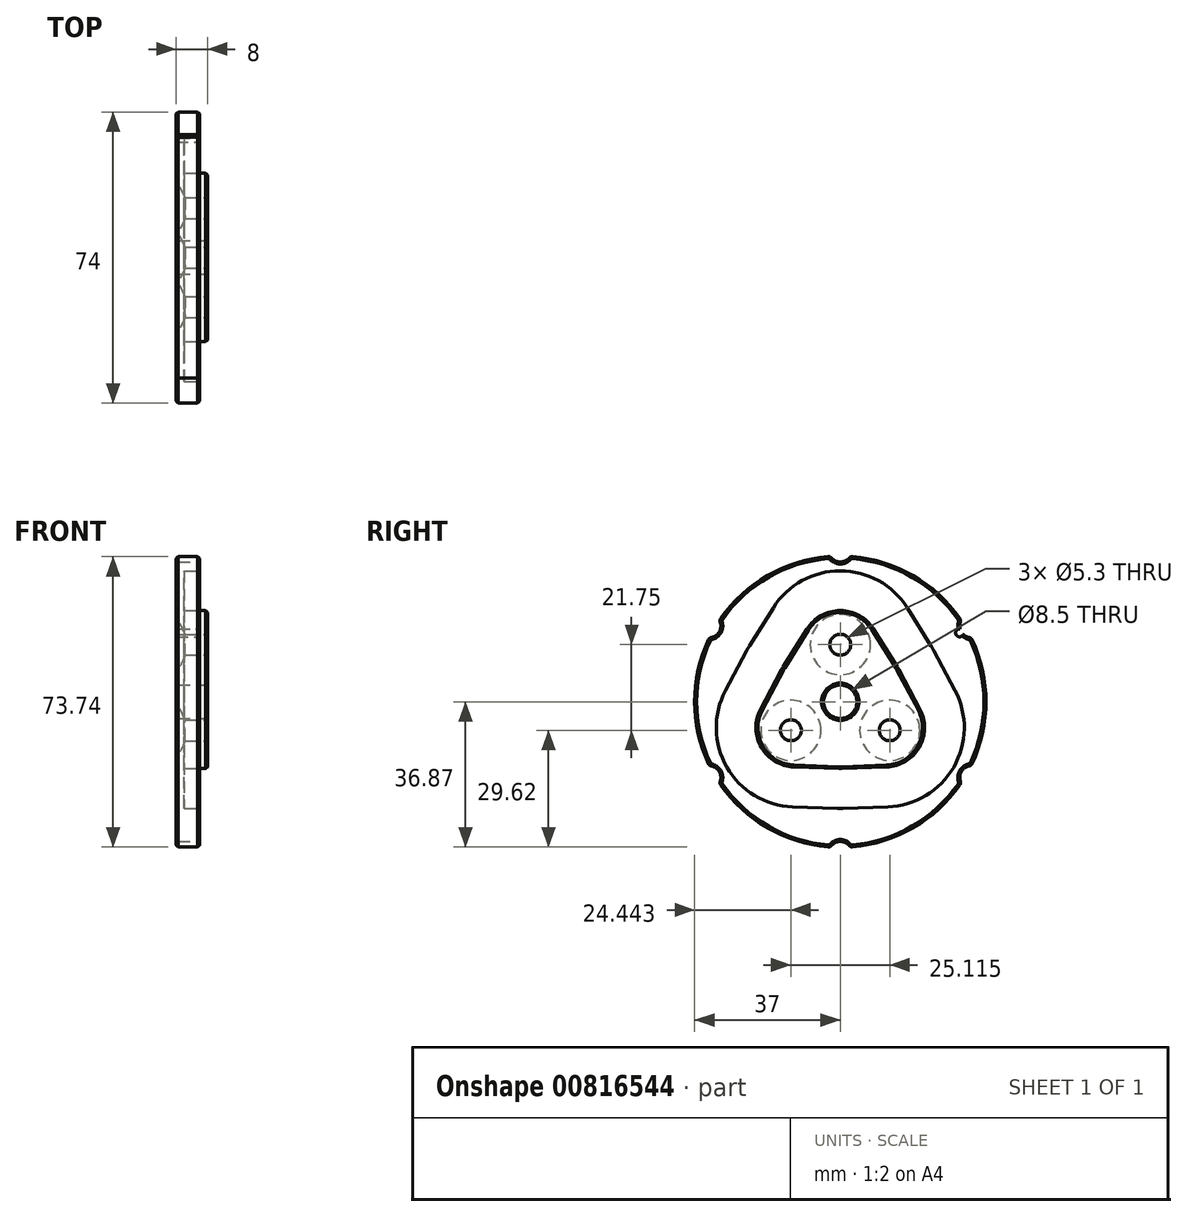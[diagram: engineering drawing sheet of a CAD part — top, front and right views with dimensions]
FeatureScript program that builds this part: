
annotation { "Feature Type Name" : "Feature", "Feature Type Description" : "" }
export const myFeature = defineFeature(function(context is Context, id is Id, definition is map)
    precondition{}
    {
        {
            var Q0;
            Q0=qCreatedBy(makeId("Right.planeOp"),FACE);
            var sketch = newSketch(context, id + "F0", { "sketchPlane" : qUnion([Q0])});
            skArc(sketch, "E0", {"start": v(-3.09, 36.87) * mm, "mid": v(-18.5, 32.04) * mm, "end": v(-30.39, 21.1) * mm});
            skCircle(sketch, "E1", {"center": v(0, 0) * mm, "radius": 4.25 * mm});
            skLineSegment(sketch, "E2", {"start": v(0, 50.53) * mm, "end": v(0, -45.3) * mm, "construction": true});
            skLineSegment(sketch, "E3", {"start": v(0, 0) * mm, "end": v(28.08, 48.64) * mm, "construction": true});
            skLineSegment(sketch, "E4", {"start": v(0, 0) * mm, "end": v(48.73, -28.13) * mm, "construction": true});
            skLineSegment(sketch, "E5.MirrorCS", {"start": v(0, 0) * mm, "end": v(-28.08, 48.64) * mm, "construction": true});
            skLineSegment(sketch, "E6.MirrorCS", {"start": v(-43.76, 25.27) * mm, "end": v(32.04, -18.5) * mm, "construction": true});
            skLineSegment(sketch, "E7.MirrorCS", {"start": v(0, 0) * mm, "end": v(-28.08, -48.64) * mm, "construction": true});
            skLineSegment(sketch, "E8.MirrorCS", {"start": v(0, 0) * mm, "end": v(28.08, -48.64) * mm, "construction": true});
            skLineSegment(sketch, "E9", {"start": v(-8.48, 18.48) * mm, "end": v(-14.54, 8.81) * mm});
            skLineSegment(sketch, "E10", {"start": v(-14.9, 8.18) * mm, "end": v(-20.25, -1.9) * mm});
            skLineSegment(sketch, "E11", {"start": v(-11.78, -16.58) * mm, "end": v(-0.36, -17) * mm});
            skLineSegment(sketch, "E12", {"start": v(0.36, -17) * mm, "end": v(11.77, -16.58) * mm});
            skLineSegment(sketch, "E13", {"start": v(20.24, -1.9) * mm, "end": v(14.9, 8.18) * mm});
            skLineSegment(sketch, "E14", {"start": v(14.53, 8.8) * mm, "end": v(8.47, 18.48) * mm});
            skPoint(sketch, "E15.visualSharp", {"position": v(0, 32) * mm});
            skArc(sketch, "E15.filletArc", {"start": v(8.47, 18.48) * mm, "mid": v(0, 23.17) * mm, "end": v(-8.48, 18.48) * mm});
            skPoint(sketch, "E16.visualSharp", {"position": v(-14.73, 8.5) * mm});
            skArc(sketch, "E16.filletArc", {"start": v(-14.54, 8.81) * mm, "mid": v(-14.73, 8.5) * mm, "end": v(-14.9, 8.18) * mm});
            skPoint(sketch, "E17.visualSharp", {"position": v(-27.71, -16) * mm});
            skArc(sketch, "E17.filletArc", {"start": v(-20.25, -1.9) * mm, "mid": v(-20.07, -11.59) * mm, "end": v(-11.78, -16.58) * mm});
            skPoint(sketch, "E18.visualSharp", {"position": v(0, -17.01) * mm});
            skArc(sketch, "E18.filletArc", {"start": v(-0.36, -17) * mm, "mid": v(0, -17) * mm, "end": v(0.36, -17) * mm});
            skPoint(sketch, "E19.visualSharp", {"position": v(27.71, -16) * mm});
            skArc(sketch, "E19.filletArc", {"start": v(11.77, -16.58) * mm, "mid": v(20.07, -11.59) * mm, "end": v(20.24, -1.9) * mm});
            skPoint(sketch, "E20.visualSharp", {"position": v(14.72, 8.5) * mm});
            skArc(sketch, "E20.filletArc", {"start": v(14.9, 8.18) * mm, "mid": v(14.72, 8.5) * mm, "end": v(14.53, 8.8) * mm});
            skLineSegment(sketch, "E21.0", {"start": v(-17.03, 23.85) * mm, "end": v(-23.1, 14.18) * mm});
            skArc(sketch, "E21.1", {"start": v(-0.73, -27.1) * mm, "mid": v(0, -27.1) * mm, "end": v(0.73, -27.1) * mm});
            skLineSegment(sketch, "E21.2", {"start": v(-12.14, -26.67) * mm, "end": v(-0.73, -27.1) * mm});
            skArc(sketch, "E21.3", {"start": v(-29.17, 2.82) * mm, "mid": v(-28.82, -16.64) * mm, "end": v(-12.14, -26.67) * mm});
            skLineSegment(sketch, "E21.4", {"start": v(-23.83, 12.91) * mm, "end": v(-29.17, 2.82) * mm});
            skLineSegment(sketch, "E21.5", {"start": v(0.73, -27.1) * mm, "end": v(12.14, -26.68) * mm});
            skArc(sketch, "E21.6", {"start": v(-23.1, 14.18) * mm, "mid": v(-23.47, 13.55) * mm, "end": v(-23.83, 12.91) * mm});
            skArc(sketch, "E21.7", {"start": v(12.14, -26.68) * mm, "mid": v(28.81, -16.63) * mm, "end": v(29.16, 2.83) * mm});
            skLineSegment(sketch, "E21.8", {"start": v(29.16, 2.83) * mm, "end": v(23.81, 12.91) * mm});
            skArc(sketch, "E21.9", {"start": v(23.81, 12.91) * mm, "mid": v(23.46, 13.55) * mm, "end": v(23.09, 14.17) * mm});
            skLineSegment(sketch, "E21.10", {"start": v(23.09, 14.17) * mm, "end": v(17.03, 23.84) * mm});
            skArc(sketch, "E21.11", {"start": v(17.03, 23.84) * mm, "mid": v(0, 33.27) * mm, "end": v(-17.03, 23.85) * mm});
            skCircle(sketch, "E22", {"center": v(0, 0) * mm, "radius": 14.5 * mm, "construction": true});
            skCircle(sketch, "E23", {"center": v(-12.56, -7.25) * mm, "radius": 2.65 * mm});
            skCircle(sketch, "E24", {"center": v(12.56, -7.25) * mm, "radius": 2.65 * mm});
            skCircle(sketch, "E25", {"center": v(0, 14.5) * mm, "radius": 2.65 * mm});
            skArc(sketch, "E26", {"start": v(30.45, 18.5) * mm, "mid": v(29.44, 17) * mm, "end": v(31.24, 17.13) * mm});
            skArc(sketch, "E27", {"start": v(-2.25, 36.53) * mm, "mid": v(0, 35.5) * mm, "end": v(2.25, 36.53) * mm});
            skPoint(sketch, "E28.visualSharp", {"position": v(-2.53, 36.91) * mm});
            skArc(sketch, "E28.filletArc", {"start": v(-2.25, 36.53) * mm, "mid": v(-2.63, 36.8) * mm, "end": v(-3.09, 36.87) * mm});
            skPoint(sketch, "E29.visualSharp", {"position": v(2.53, 36.91) * mm});
            skArc(sketch, "E29.filletArc", {"start": v(3.09, 36.87) * mm, "mid": v(2.63, 36.8) * mm, "end": v(2.25, 36.53) * mm});
            skPoint(sketch, "E30.center.orphan", {"position": v(0, -35) * mm});
            skArc(sketch, "E31.MirrorCS", {"start": v(32.76, 16.32) * mm, "mid": v(33.19, 16.12) * mm, "end": v(33.48, 15.76) * mm});
            skArc(sketch, "E32.MirrorCS", {"start": v(30.39, 21.1) * mm, "mid": v(30.56, 20.68) * mm, "end": v(30.51, 20.22) * mm});
            skPoint(sketch, "E33.MirrorP", {"position": v(33.23, 16.26) * mm});
            skArc(sketch, "E34.MirrorCS", {"start": v(32.76, 16.32) * mm, "mid": v(31.94, 16.6) * mm, "end": v(31.24, 17.13) * mm});
            skPoint(sketch, "E35.MirrorP", {"position": v(30.7, 20.65) * mm});
            skArc(sketch, "E36.trimOffspring", {"start": v(30.39, 21.1) * mm, "mid": v(18.5, 32.04) * mm, "end": v(3.09, 36.87) * mm});
            skLineSegment(sketch, "E37.trimOffspring", {"start": v(31.18, 18) * mm, "end": v(-39.22, -22.65) * mm, "construction": true});
            skArc(sketch, "E38.trimOffspring", {"start": v(30.45, 18.5) * mm, "mid": v(30.35, 19.36) * mm, "end": v(30.51, 20.22) * mm});
            skArc(sketch, "E39.MirrorCS", {"start": v(-30.51, 20.22) * mm, "mid": v(-30.56, 20.68) * mm, "end": v(-30.39, 21.1) * mm});
            skArc(sketch, "E40.MirrorCS", {"start": v(-33.48, 15.76) * mm, "mid": v(-33.19, 16.12) * mm, "end": v(-32.76, 16.32) * mm});
            skPoint(sketch, "E41.MirrorP", {"position": v(-33.23, 16.26) * mm});
            skPoint(sketch, "E42.MirrorP", {"position": v(-30.7, 20.65) * mm});
            skArc(sketch, "E43.MirrorCS", {"start": v(-30.51, 20.22) * mm, "mid": v(-30.75, 17.75) * mm, "end": v(-32.76, 16.32) * mm});
            skArc(sketch, "E44.trimOffspring", {"start": v(-33.48, 15.76) * mm, "mid": v(-37, 0) * mm, "end": v(-33.48, -15.76) * mm});
            skArc(sketch, "E45.MirrorCS", {"start": v(-33.48, -15.76) * mm, "mid": v(-33.19, -16.12) * mm, "end": v(-32.76, -16.32) * mm});
            skArc(sketch, "E46.MirrorCS", {"start": v(-30.51, -20.22) * mm, "mid": v(-30.56, -20.68) * mm, "end": v(-30.39, -21.1) * mm});
            skPoint(sketch, "E47.MirrorP", {"position": v(-30.7, -20.65) * mm});
            skArc(sketch, "E48.MirrorCS", {"start": v(-30.51, -20.22) * mm, "mid": v(-30.75, -17.75) * mm, "end": v(-32.76, -16.32) * mm});
            skPoint(sketch, "E49.MirrorP", {"position": v(-33.23, -16.26) * mm});
            skArc(sketch, "E50.trimOffspring", {"start": v(-30.39, -21.1) * mm, "mid": v(-18.5, -32.04) * mm, "end": v(-3.09, -36.87) * mm});
            skArc(sketch, "E51.MirrorCS", {"start": v(3.09, -36.87) * mm, "mid": v(2.63, -36.8) * mm, "end": v(2.25, -36.53) * mm});
            skArc(sketch, "E52.MirrorCS", {"start": v(-2.25, -36.53) * mm, "mid": v(-2.63, -36.8) * mm, "end": v(-3.09, -36.87) * mm});
            skArc(sketch, "E53.MirrorCS", {"start": v(-2.25, -36.53) * mm, "mid": v(0, -35.5) * mm, "end": v(2.25, -36.53) * mm});
            skPoint(sketch, "E54.MirrorP", {"position": v(-2.53, -36.91) * mm});
            skPoint(sketch, "E55.MirrorP", {"position": v(2.53, -36.91) * mm});
            skArc(sketch, "E56.trimOffspring", {"start": v(3.09, -36.87) * mm, "mid": v(18.5, -32.04) * mm, "end": v(30.39, -21.1) * mm});
            skPoint(sketch, "E57.orphan", {"position": v(39.22, -22.65) * mm});
            skPoint(sketch, "E58.MirrorCS.start.orphan", {"position": v(43.76, 25.27) * mm});
            skArc(sketch, "E59.MirrorCS", {"start": v(30.39, -21.1) * mm, "mid": v(30.56, -20.68) * mm, "end": v(30.51, -20.22) * mm});
            skArc(sketch, "E60.MirrorCS", {"start": v(32.76, -16.32) * mm, "mid": v(33.19, -16.12) * mm, "end": v(33.48, -15.76) * mm});
            skPoint(sketch, "E61.MirrorP", {"position": v(33.23, -16.26) * mm});
            skPoint(sketch, "E62.MirrorP", {"position": v(30.7, -20.65) * mm});
            skPoint(sketch, "E63.MirrorP", {"position": v(30.31, -17.5) * mm});
            skArc(sketch, "E64.MirrorCS", {"start": v(32.76, -16.32) * mm, "mid": v(30.75, -17.75) * mm, "end": v(30.51, -20.22) * mm});
            skArc(sketch, "E65.trimOffspring", {"start": v(33.48, -15.76) * mm, "mid": v(37, 0) * mm, "end": v(33.48, 15.76) * mm});
            skSolve(sketch);
        }
        {
            var Q0;
            Q0=qSketchRegion(id+"F0",true);
            var Q1;
            Q1=makeQuery(id+"F0.imprint","IMPRINT",FACE,{"disambiguationData":[TD([[makeQuery(id+"F0.imprint","IMPRINT",EDGE,{"derivedFrom":sQuery(id+"F0.wireOp",EDGE,"E9")}),-1.0]])]});
            var Q2;
            Q2=makeQuery(id+"F0.imprint","IMPRINT",FACE,{"disambiguationData":[TD([[makeQuery(id+"F0.imprint","IMPRINT",EDGE,{"derivedFrom":sQuery(id+"F0.wireOp",EDGE,"E1")}),-1.0]])]});
            extrude(context, id + "F1", {"entities" : qUnion([Q0, Q1, Q2]), "oppositeDirection" : true, "depth" : 6 * mm, "offsetDistance" : 25 * mm});
        }
        {
            var Q0;
            Q0=makeQuery(id+"F0.imprint","IMPRINT",FACE,{"disambiguationData":[TD([[makeQuery(id+"F0.imprint","IMPRINT",EDGE,{"derivedFrom":sQuery(id+"F0.wireOp",EDGE,"E9")}),-1.0]])]});
            extrude(context, id + "F2", {"entities" : qUnion([Q0]), "operationType" : NewBodyOperationType.REMOVE, "oppositeDirection" : true, "depth" : 4 * mm, "offsetDistance" : 25 * mm});
        }
        {
            var Q0;
            {var subQ0=sQuery(id+"F0.wireOp",EDGE,"E1");Q0=makeQuery(id+"F2.boolean.opBoolean","SPLIT",FACE,{"disambiguationData":[TD([makeQuery(id+"F1.opExtrude","SWEPT_FACE",FACE,{"disambiguationData":[OSD([subQ0])]})])],"derivedFrom":makeQuery(id+"F1.opExtrude","CAP_FACE",FACE,{"disambiguationData":[OSD([sQuery(id+"F0.wireOp",EDGE,"E0"),subQ0])],"isStart":true})});}
            extrude(context, id + "F3", {"entities" : qUnion([Q0]), "operationType" : NewBodyOperationType.ADD, "depth" : 2 * mm, "offsetDistance" : 25 * mm});
        }
        {
            var Q0;
            Q0=makeQuery(id+"FyIsF6kSJw19HWJ_1.boolean.opBoolean","COPY",EDGE,{"derivedFrom":makeQuery(id+"FyIsF6kSJw19HWJ_1.opExtrude","CAP_EDGE",EDGE,{"disambiguationData":[OSD([sQuery(id+"F7LV2Zl85KT3uEW_1.wireOp",EDGE,"4heGY6iT-OKOq-OImW-84Io-U2CDUhAUHW4h")])],"isStart":true})});
            var Q1;
            Q1=makeQuery(id+"F1.opExtrude","CAP_EDGE",EDGE,{"disambiguationData":[OSD([sQuery(id+"F0.wireOp",EDGE,"E56.trimOffspring")])],"isStart":false});
            var Q2;
            Q2=makeQuery(id+"F1.opExtrude","CAP_EDGE",EDGE,{"disambiguationData":[OSD([sQuery(id+"F0.wireOp",EDGE,"E56.trimOffspring")])],"isStart":true});
            var Q3;
            Q3=makeQuery(id+"F2.boolean.opBoolean","COPY",EDGE,{"derivedFrom":makeQuery(id+"F2.opExtrude","CAP_EDGE",EDGE,{"disambiguationData":[OSD([sQuery(id+"F0.wireOp",EDGE,"E21.7")])],"isStart":true})});
            var Q4;
            Q4=makeQuery(id+"F3.opExtrude","CAP_EDGE",EDGE,{"disambiguationData":[OSD([sQuery(id+"F0.wireOp",EDGE,"E19.filletArc")])],"isStart":false});
            var Q5;
            Q5=makeQuery(id+"F3.opExtrude","CAP_EDGE",EDGE,{"disambiguationData":[OSD([sQuery(id+"F0.wireOp",EDGE,"E1")])],"isStart":false});
            var Q6;
            Q6=makeQuery(id+"FyIsF6kSJw19HWJ_1.boolean.opBoolean","COPY",EDGE,{"derivedFrom":makeQuery(id+"FyIsF6kSJw19HWJ_1.opExtrude","CAP_EDGE",EDGE,{"disambiguationData":[OSD([sQuery(id+"F0.wireOp",EDGE,"E1")])],"isStart":false})});
            chamfer(context, id + "F4", {"entities" : qUnion([Q0, Q1, Q2, Q3, Q4, Q5, Q6]), "width" : 0.5 * mm, "tangentPropagation" : true});
        }
        {
            var Q0;
            Q0=makeQuery(id+"F1.opExtrude","CAP_EDGE",EDGE,{"disambiguationData":[OSD([sQuery(id+"F0.wireOp",EDGE,"E25")])],"isStart":false});
            var Q1;
            Q1=makeQuery(id+"F1.opExtrude","CAP_EDGE",EDGE,{"disambiguationData":[OSD([sQuery(id+"F0.wireOp",EDGE,"E23")])],"isStart":false});
            var Q2;
            Q2=makeQuery(id+"F1.opExtrude","CAP_EDGE",EDGE,{"disambiguationData":[OSD([sQuery(id+"F0.wireOp",EDGE,"E24")])],"isStart":false});
            chamfer(context, id + "F5", {"entities" : qUnion([Q0, Q1, Q2]), "chamferType" : ChamferType.TWO_OFFSETS, "width1" : 5 * mm, "oppositeDirection" : false, "width2" : 2.3 * mm, "tangentPropagation" : true});
        }
        {
            var Q0;
            Q0=makeQuery(id+"F1.opExtrude","CAP_EDGE",EDGE,{"disambiguationData":[OSD([sQuery(id+"F0.wireOp",EDGE,"E1")])],"isStart":false});
            chamfer(context, id + "F6", {"entities" : qUnion([Q0]), "width" : 0.5 * mm, "tangentPropagation" : true});
        }
    });
